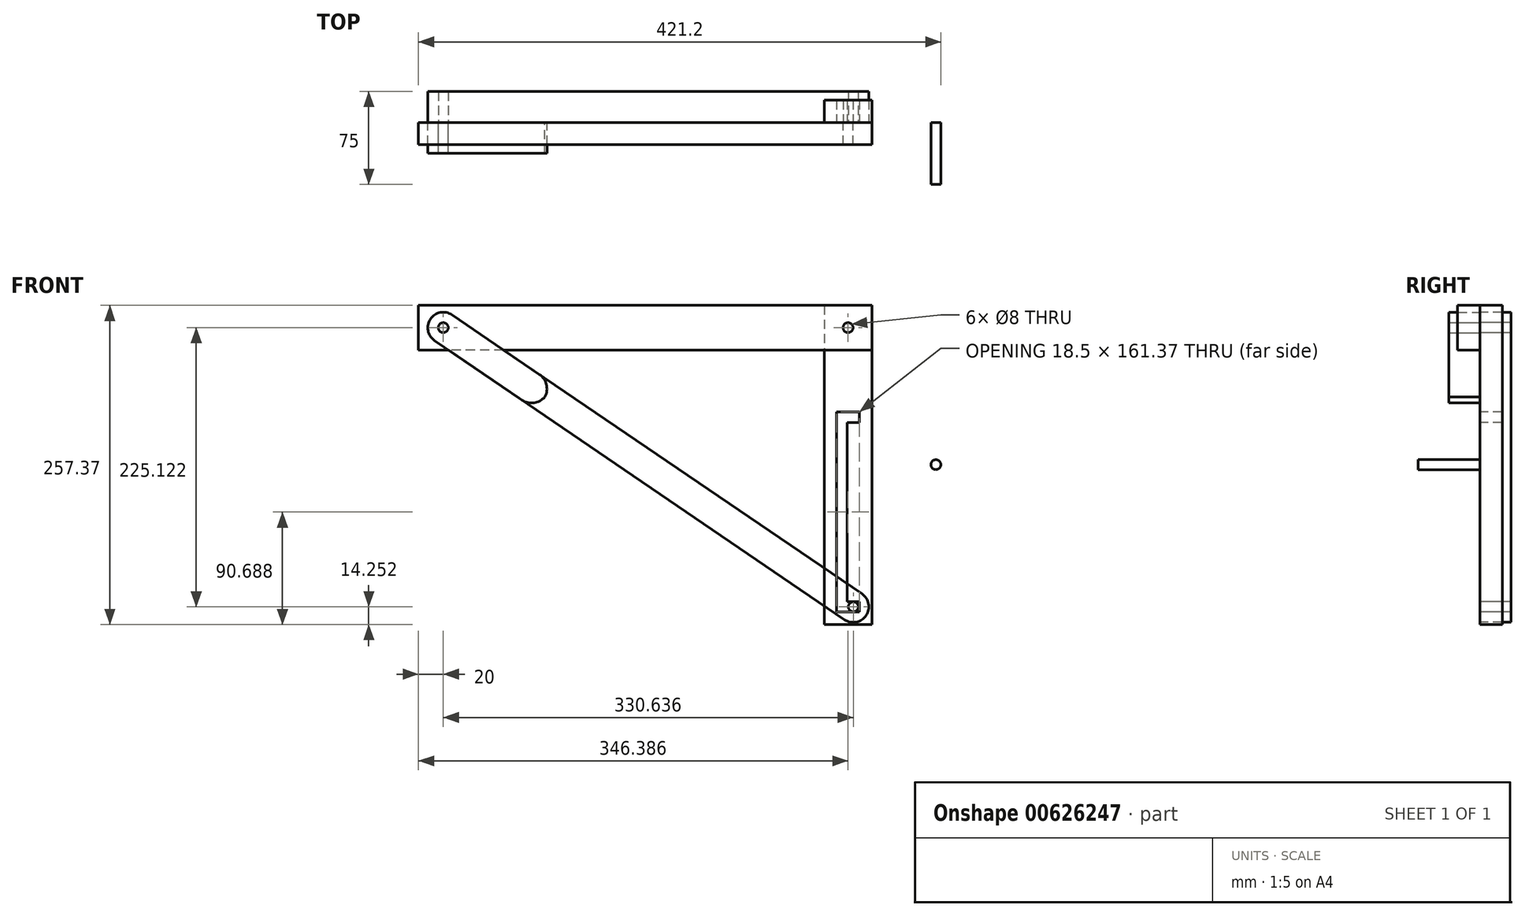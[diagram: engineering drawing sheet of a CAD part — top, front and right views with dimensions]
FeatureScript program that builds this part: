
annotation { "Feature Type Name" : "Feature", "Feature Type Description" : "" }
export const myFeature = defineFeature(function(context is Context, id is Id, definition is map)
    precondition{}
    {
        {
            var Q0;
            Q0=qCreatedBy(makeId("Front.planeOp"),FACE);
            var sketch = newSketch(context, id + "F0", { "sketchPlane" : qUnion([Q0])});
            skLineSegment(sketch, "E0.bottom", {"start": v(-39.2, 81.82) * mm, "end": v(-0.7, 81.82) * mm});
            skLineSegment(sketch, "E0.top", {"start": v(-39.2, -175.55) * mm, "end": v(-0.7, -175.55) * mm});
            skLineSegment(sketch, "E0.left", {"start": v(-39.2, 81.82) * mm, "end": v(-39.2, -175.55) * mm});
            skLineSegment(sketch, "E0.right", {"start": v(-0.7, 81.82) * mm, "end": v(-0.7, -175.55) * mm});
            skCircle(sketch, "E1", {"center": v(-19.94, 63.82) * mm, "radius": 4 * mm});
            skPoint(sketch, "E1.centerSnap0", {"position": v(-19.94, 81.82) * mm});
            skLineSegment(sketch, "E2.bottom", {"start": v(-0.7, 81.82) * mm, "end": v(-366.33, 81.82) * mm});
            skLineSegment(sketch, "E2.top", {"start": v(-0.7, 45.82) * mm, "end": v(-366.33, 45.82) * mm});
            skLineSegment(sketch, "E2.left", {"start": v(-0.7, 81.82) * mm, "end": v(-0.7, 45.82) * mm});
            skLineSegment(sketch, "E2.right", {"start": v(-366.33, 81.82) * mm, "end": v(-366.33, 45.82) * mm});
            skCircle(sketch, "E3", {"center": v(-346.33, 63.82) * mm, "radius": 4 * mm});
            skPoint(sketch, "E3.centerSnap0", {"position": v(-366.33, 63.82) * mm});
            skLineSegment(sketch, "E4.bottom", {"start": v(-7.44, 45.82) * mm, "end": v(-43.44, 45.82) * mm, "construction": true});
            skLineSegment(sketch, "E4.top", {"start": v(-7.44, 411.46) * mm, "end": v(-43.44, 411.46) * mm, "construction": true});
            skLineSegment(sketch, "E4.left", {"start": v(-7.44, 45.82) * mm, "end": v(-7.44, 411.46) * mm, "construction": true});
            skLineSegment(sketch, "E4.right", {"start": v(-43.44, 45.82) * mm, "end": v(-43.44, 411.46) * mm, "construction": true});
            skCircle(sketch, "E5", {"center": v(-25.17, 391.46) * mm, "radius": 3.78 * mm, "construction": true});
            skLineSegment(sketch, "E6", {"start": v(-25.17, 391.46) * mm, "end": v(-25.44, 411.46) * mm, "construction": true});
            skLineSegment(sketch, "E7", {"start": v(-346.33, 63.82) * mm, "end": v(-366.33, 63.82) * mm, "construction": true});
            skLineSegment(sketch, "E8", {"start": v(-19.94, 63.82) * mm, "end": v(-0.7, 63.82) * mm, "construction": true});
            skLineSegment(sketch, "E9", {"start": v(-19.94, 63.82) * mm, "end": v(-19.94, 45.82) * mm, "construction": true});
            skLineSegment(sketch, "E10", {"start": v(-19.94, 63.82) * mm, "end": v(-346.33, 63.82) * mm, "construction": true});
            skLineSegment(sketch, "E11", {"start": v(-10.7, -4.18) * mm, "end": v(-29.2, -4.18) * mm});
            skLineSegment(sketch, "E12", {"start": v(-29.2, -4.18) * mm, "end": v(-29.2, -165.55) * mm});
            skLineSegment(sketch, "E13", {"start": v(-29.2, -165.55) * mm, "end": v(-10.7, -165.55) * mm});
            skLineSegment(sketch, "E14", {"start": v(-10.7, -165.55) * mm, "end": v(-10.7, -157.05) * mm});
            skLineSegment(sketch, "E15", {"start": v(-10.7, -157.05) * mm, "end": v(-20.7, -157.05) * mm});
            skLineSegment(sketch, "E16", {"start": v(-20.7, -157.05) * mm, "end": v(-20.7, -12.68) * mm});
            skLineSegment(sketch, "E17", {"start": v(-20.7, -12.68) * mm, "end": v(-10.7, -12.68) * mm});
            skLineSegment(sketch, "E18", {"start": v(-10.7, -12.68) * mm, "end": v(-10.7, -4.18) * mm});
            skCircle(sketch, "E19", {"center": v(-15.7, -161.3) * mm, "radius": 4 * mm});
            skPoint(sketch, "E19.centerSnap0", {"position": v(-10.7, -161.3) * mm});
            skPoint(sketch, "E19.centerSnap1", {"position": v(-15.7, -157.05) * mm});
            skLineSegment(sketch, "E20", {"start": v(-15.7, -161.3) * mm, "end": v(-346.33, 63.82) * mm, "construction": true});
            skCircle(sketch, "E21", {"center": v(-15.7, -8.43) * mm, "radius": 4 * mm, "construction": true});
            skPoint(sketch, "E21.centerSnap0", {"position": v(-10.7, -8.43) * mm});
            skPoint(sketch, "E21.centerSnap1", {"position": v(-15.7, -12.68) * mm});
            skLineSegment(sketch, "E22", {"start": v(-25.17, 391.46) * mm, "end": v(-15.7, -8.43) * mm, "construction": true});
            skArc(sketch, "E23.0.startCap", {"start": v(-8.66, -150.97) * mm, "mid": v(-5.36, -168.33) * mm, "end": v(-22.73, -171.63) * mm});
            skArc(sketch, "E23.0.endCap", {"start": v(-353.36, 53.5) * mm, "mid": v(-356.66, 70.86) * mm, "end": v(-339.3, 74.16) * mm});
            skLineSegment(sketch, "E23.0.left", {"start": v(-22.73, -171.63) * mm, "end": v(-353.36, 53.5) * mm});
            skLineSegment(sketch, "E23.0.right", {"start": v(-8.66, -150.97) * mm, "end": v(-339.3, 74.16) * mm});
            skLineSegment(sketch, "E24", {"start": v(-271.34, -2.35) * mm, "end": v(-257.27, 18.31) * mm});
            skSolve(sketch);
        }
        {
            var Q0;
            Q0=makeQuery(id+"F0.imprint","IMPRINT",FACE,{"disambiguationData":[TD([[makeQuery(id+"F0.imprint","IMPRINT",EDGE,{"derivedFrom":sQuery(id+"F0.wireOp",EDGE,"E1")}),-1.0]])]});
            var Q1;
            {var subQ0=sQuery(id+"F0.wireOp",EDGE,"E0.top");Q1=makeQuery(id+"F0.imprint","IMPRINT",FACE,{"disambiguationData":[TD([[makeQuery(id+"F0.imprint","IMPRINT",EDGE,{"derivedFrom":subQ0}),1.0]])]});}
            var Q2;
            {var subQ4=sQuery(id+"F0.wireOp",EDGE,"E13");Q2=makeQuery(id+"F0.imprint","IMPRINT",FACE,{"disambiguationData":[TD([[makeQuery(id+"F0.imprint","IMPRINT",EDGE,{"derivedFrom":subQ4}),-1.0]])]});}
            extrude(context, id + "F1", {"entities" : qUnion([Q0, Q1, Q2]), "oppositeDirection" : true, "depth" : 18 * mm, "offsetDistance" : 25 * mm});
        }
        {
            var Q0;
            {var subQ0=sQuery(id+"F0.wireOp",EDGE,"E2.right");Q0=makeQuery(id+"F0.imprint","IMPRINT",FACE,{"disambiguationData":[TD([[makeQuery(id+"F0.imprint","IMPRINT",EDGE,{"derivedFrom":subQ0}),1.0]])]});}
            var Q1;
            Q1=makeQuery(id+"F0.imprint","IMPRINT",FACE,{"disambiguationData":[TD([[makeQuery(id+"F0.imprint","IMPRINT",EDGE,{"derivedFrom":sQuery(id+"F0.wireOp",EDGE,"E1")}),-1.0]])]});
            var Q2;
            Q2=makeQuery(id+"F0.imprint","IMPRINT",FACE,{"disambiguationData":[TD([[makeQuery(id+"F0.imprint","IMPRINT",EDGE,{"derivedFrom":sQuery(id+"F0.wireOp",EDGE,"E3")}),-1.0]])]});
            extrude(context, id + "F2", {"entities" : qUnion([Q0, Q1, Q2]), "depth" : 18 * mm, "offsetDistance" : 25 * mm});
        }
        {
            var Q0;
            {var subQ4=sQuery(id+"F0.wireOp",EDGE,"E13");Q0=makeQuery(id+"F0.imprint","IMPRINT",FACE,{"disambiguationData":[TD([[makeQuery(id+"F0.imprint","IMPRINT",EDGE,{"derivedFrom":subQ4}),-1.0]])]});}
            var Q1;
            {var subQ0=sQuery(id+"F0.wireOp",EDGE,"E23.0.left");var subQ1=sQuery(id+"F0.wireOp",EDGE,"E0.left");var subQ2=makeQuery(id+"F0.imprint","INTERSECT",VERTEX,{"derivedFrom":[subQ1,subQ0]});Q1=makeQuery(id+"F0.imprint","IMPRINT",FACE,{"disambiguationData":[TD([[makeQuery(id+"F0.imprint","IMPRINT",EDGE,{"disambiguationData":[TD([[subQ2,1.0]])],"derivedFrom":subQ1}),-1.0]])]});}
            var Q2;
            {var subQ6=sQuery(id+"F0.wireOp",EDGE,"E13");Q2=makeQuery(id+"F0.imprint","IMPRINT",FACE,{"disambiguationData":[TD([[makeQuery(id+"F0.imprint","IMPRINT",EDGE,{"derivedFrom":subQ6}),1.0]])]});}
            var Q3;
            Q3=makeQuery(id+"F0.imprint","IMPRINT",FACE,{"disambiguationData":[TD([[makeQuery(id+"F0.imprint","IMPRINT",EDGE,{"derivedFrom":sQuery(id+"F0.wireOp",EDGE,"E3")}),-1.0]])]});
            var Q4;
            {var subQ5=sQuery(id+"F0.wireOp",EDGE,"E24");Q4=makeQuery(id+"F0.imprint","IMPRINT",FACE,{"disambiguationData":[TD([[makeQuery(id+"F0.imprint","IMPRINT",EDGE,{"derivedFrom":subQ5}),1.0]])]});}
            extrude(context, id + "F3", {"entities" : qUnion([Q0, Q1, Q2, Q3, Q4]), "oppositeDirection" : true, "depth" : 25 * mm, "offsetDistance" : 25 * mm});
        }
        {
            var Q0;
            Q0=qCreatedBy(makeId("Front.planeOp"),FACE);
            var sketch = newSketch(context, id + "F4", { "sketchPlane" : qUnion([Q0])});
            skCircle(sketch, "E25", {"center": v(50.87, -46.65) * mm, "radius": 4 * mm});
            skSolve(sketch);
        }
        {
            var Q0;
            Q0 = qSketchRegion(id + "F4", true);
            extrude(context, id + "F5", {"entities" : qUnion([Q0]), "depth" : 50 * mm, "offsetDistance" : 25 * mm});
        }
        {
            var Q0;
            {var subQ5=sQuery(id+"F0.wireOp",EDGE,"E24");Q0=makeQuery(id+"F0.imprint","IMPRINT",FACE,{"disambiguationData":[TD([[makeQuery(id+"F0.imprint","IMPRINT",EDGE,{"derivedFrom":subQ5}),1.0]])]});}
            var Q1;
            Q1=makeQuery(id+"F0.imprint","IMPRINT",FACE,{"disambiguationData":[TD([[makeQuery(id+"F0.imprint","IMPRINT",EDGE,{"derivedFrom":sQuery(id+"F0.wireOp",EDGE,"E3")}),-1.0]])]});
            extrude(context, id + "F6", {"entities" : qUnion([Q0, Q1]), "depth" : 25 * mm, "offsetDistance" : 25 * mm});
        }
        {
            var Q0;
            Q0=makeQuery(id+"F6.opExtrude","SWEPT_EDGE",EDGE,{"disambiguationData":[OSD([sQuery(id+"F0.wireOp",EDGE,"E23.0.right"),sQuery(id+"F0.wireOp",EDGE,"E24")])]});
            var Q1;
            Q1=makeQuery(id+"F6.opExtrude","SWEPT_EDGE",EDGE,{"disambiguationData":[OSD([sQuery(id+"F0.wireOp",EDGE,"E23.0.left"),sQuery(id+"F0.wireOp",EDGE,"E24")])]});
            fillet(context, id + "F7", {"entities" : qUnion([Q0, Q1]), "radius" : 14 * mm, "tangentPropagation" : true, "allowEdgeOverflow" : false});
        }
    });
